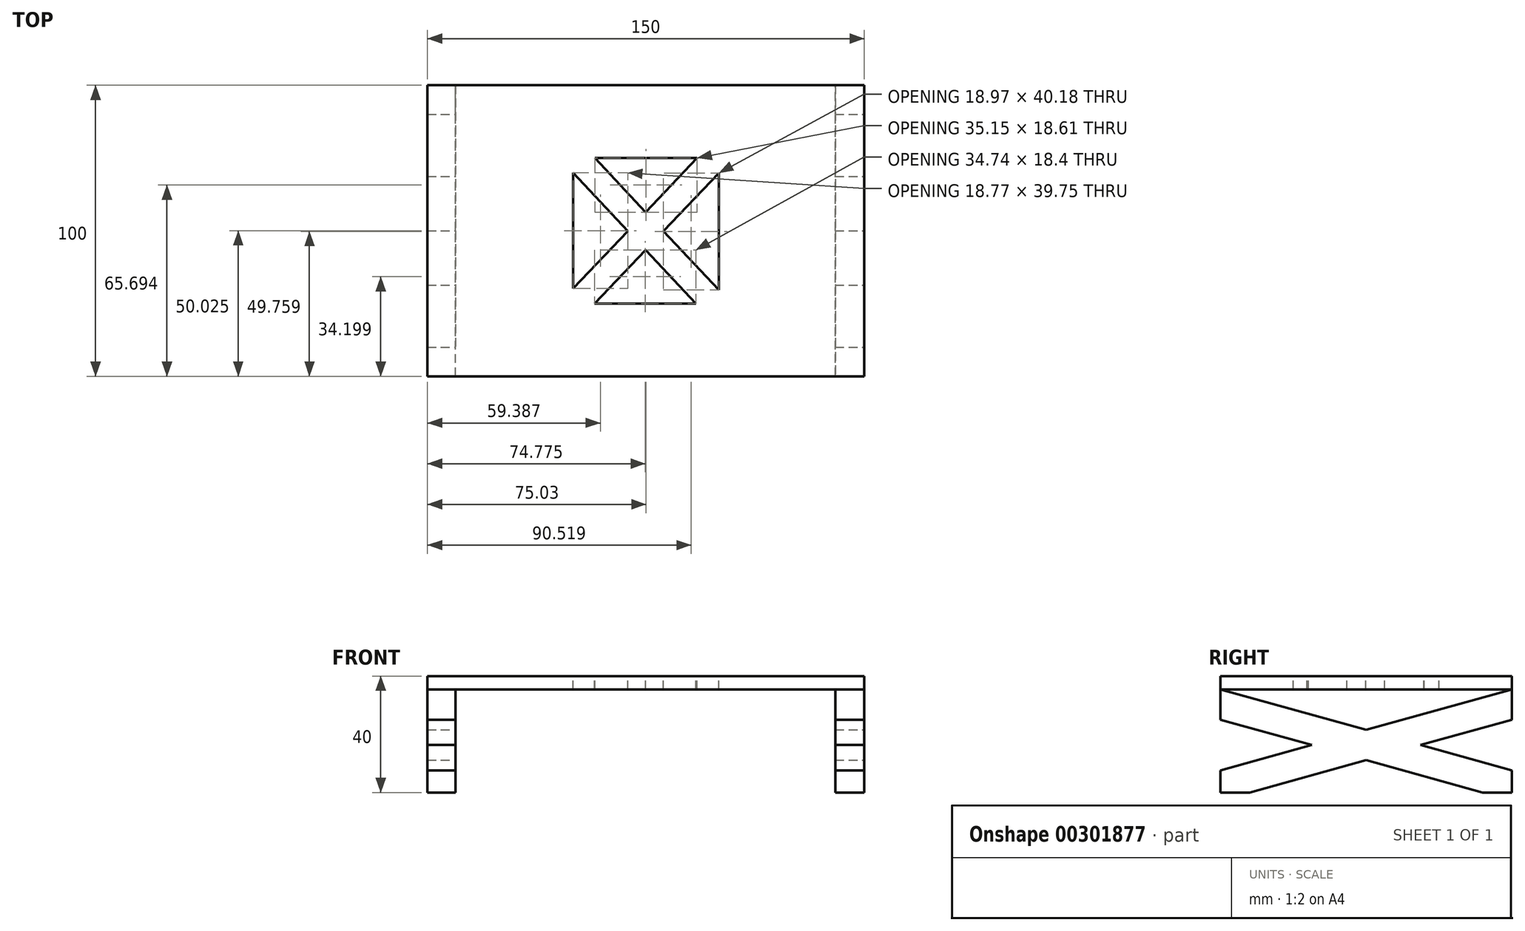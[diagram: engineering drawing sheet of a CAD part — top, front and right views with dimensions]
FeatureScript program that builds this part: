
annotation { "Feature Type Name" : "Feature", "Feature Type Description" : "" }
export const myFeature = defineFeature(function(context is Context, id is Id, definition is map)
    precondition{}
    {
        {
            var Q0;
            Q0=qCreatedBy(makeId("Front.planeOp"),FACE);
            var sketch = newSketch(context, id + "F0", { "sketchPlane" : qUnion([Q0])});
            skLineSegment(sketch, "E0.bottom", {"start": v(-768.36, 54.12) * mm, "end": v(731.64, 54.12) * mm});
            skLineSegment(sketch, "E0.top", {"start": v(-768.36, -345.88) * mm, "end": v(731.64, -345.88) * mm});
            skLineSegment(sketch, "E0.left", {"start": v(-768.36, 54.12) * mm, "end": v(-768.36, -345.88) * mm});
            skLineSegment(sketch, "E0.right", {"start": v(731.64, 54.12) * mm, "end": v(731.64, -345.88) * mm});
            skSolve(sketch);
        }
        {
            var Q0;
            Q0=qSketchRegion(id+"F0",true);
            extrude(context, id + "F1", {"entities" : qUnion([Q0]), "depth" : 1000 * mm});
        }
        {
            var Q0;
            Q0=makeQuery(id+"F1.opExtrude","SWEPT_FACE",FACE,{"disambiguationData":[OSD([sQuery(id+"F0.wireOp",EDGE,"E0.right")])]});
            var sketch = newSketch(context, id + "F2", { "sketchPlane" : qUnion([Q0])});
            skLineSegment(sketch, "E1", {"start": v(-900, -345.88) * mm, "end": v(0, -95.88) * mm});
            skLineSegment(sketch, "E2", {"start": v(-1000, -269.87) * mm, "end": v(0, 7.9) * mm});
            skLineSegment(sketch, "E3", {"start": v(-100, -345.88) * mm, "end": v(-1000, -95.88) * mm});
            skLineSegment(sketch, "E4", {"start": v(0, -269.87) * mm, "end": v(-1000, 7.9) * mm});
            skLineSegment(sketch, "E5", {"start": v(-1000, 7.9) * mm, "end": v(0, 7.9) * mm});
            skSolve(sketch);
        }
        {
            var Q0;
            {var subQ0=sQuery(id+"F2.wireOp",EDGE,"E5");Q0=makeQuery(id+"F2.imprint","IMPRINT",FACE,{"disambiguationData":[TD([[makeQuery(id+"F2.imprint","IMPRINT",EDGE,{"derivedFrom":subQ0}),-1.0]])]});}
            var Q1;
            {var subQ0=sQuery(id+"F2.wireOp",EDGE,"E1");var subQ3=sQuery(id+"F2.wireOp",EDGE,"E3");var subQ4=makeQuery(id+"F2.imprint","INTERSECT",VERTEX,{"derivedFrom":[subQ0,subQ3]});Q1=makeQuery(id+"F2.imprint","IMPRINT",FACE,{"disambiguationData":[TD([[makeQuery(id+"F2.imprint","IMPRINT",EDGE,{"disambiguationData":[TD([[subQ4,1.0]])],"derivedFrom":subQ0}),-1.0]])]});}
            var Q2;
            {var subQ0=sQuery(id+"F2.wireOp",EDGE,"E1");var subQ1=makeQuery(id+"F1.opExtrude","CAP_EDGE",EDGE,{"disambiguationData":[OSD([sQuery(id+"F0.wireOp",EDGE,"E0.right")])],"isStart":true});var subQ2=makeQuery(id+"F2.imprint","INTERSECT",VERTEX,{"derivedFrom":[subQ1,subQ0]});Q2=makeQuery(id+"F2.imprint","IMPRINT",FACE,{"disambiguationData":[TD([[makeQuery(id+"F2.imprint","IMPRINT",EDGE,{"disambiguationData":[TD([[subQ2,1.0]])],"derivedFrom":subQ0}),-1.0]])]});}
            var Q3;
            {var subQ0=sQuery(id+"F2.wireOp",EDGE,"E2");var subQ1=makeQuery(id+"F1.opExtrude","CAP_EDGE",EDGE,{"disambiguationData":[OSD([sQuery(id+"F0.wireOp",EDGE,"E0.right")])],"isStart":false});var subQ2=makeQuery(id+"F2.imprint","INTERSECT",VERTEX,{"derivedFrom":[subQ1,subQ0]});Q3=makeQuery(id+"F2.imprint","IMPRINT",FACE,{"disambiguationData":[TD([[makeQuery(id+"F2.imprint","IMPRINT",EDGE,{"disambiguationData":[TD([[subQ2,-1.0]])],"derivedFrom":subQ0}),1.0]])]});}
            extrude(context, id + "F3", {"entities" : qUnion([Q0, Q1, Q2, Q3]), "operationType" : NewBodyOperationType.REMOVE, "endBound" : BoundingType.THROUGH_ALL, "oppositeDirection" : true, "depth" : 150 * mm});
        }
        {
            var Q0;
            Q0=makeQuery(id+"F1.opExtrude","CAP_FACE",FACE,{"disambiguationData":[OSD([sQuery(id+"F0.wireOp",EDGE,"E0.bottom"),sQuery(id+"F0.wireOp",EDGE,"E0.top"),sQuery(id+"F0.wireOp",EDGE,"E0.left"),sQuery(id+"F0.wireOp",EDGE,"E0.right")])],"isStart":false});
            var sketch = newSketch(context, id + "F4", { "sketchPlane" : qUnion([Q0])});
            skLineSegment(sketch, "E6", {"start": v(631.64, -345.88) * mm, "end": v(631.64, 8.12) * mm});
            skLineSegment(sketch, "E7", {"start": v(631.64, 8.12) * mm, "end": v(-668.36, 8.12) * mm});
            skLineSegment(sketch, "E8", {"start": v(-668.36, 8.12) * mm, "end": v(-668.36, -345.88) * mm});
            skSolve(sketch);
        }
        {
            var Q0;
            {var subQ0=sQuery(id+"F0.wireOp",EDGE,"E0.bottom");var subQ1=sQuery(id+"F0.wireOp",EDGE,"E0.right");var subQ2=sQuery(id+"F0.wireOp",EDGE,"E0.left");Q0=makeQuery(id+"F3.boolean.opBoolean","SPLIT",FACE,{"disambiguationData":[TD([makeQuery(id+"F1.opExtrude","SWEPT_FACE",FACE,{"disambiguationData":[OSD([subQ0])]})])],"derivedFrom":makeQuery(id+"F1.opExtrude","CAP_FACE",FACE,{"disambiguationData":[OSD([subQ0,sQuery(id+"F0.wireOp",EDGE,"E0.top"),subQ2,subQ1])],"isStart":true})});}
            var sketch = newSketch(context, id + "F5", { "sketchPlane" : qUnion([Q0])});
            skLineSegment(sketch, "E9.bottom", {"start": v(-631.78, 7.9) * mm, "end": v(672.17, 7.9) * mm});
            skLineSegment(sketch, "E9.top", {"start": v(-631.78, -349.34) * mm, "end": v(672.17, -349.34) * mm});
            skLineSegment(sketch, "E9.left", {"start": v(-631.78, 7.9) * mm, "end": v(-631.78, -349.34) * mm});
            skLineSegment(sketch, "E9.right", {"start": v(672.17, 7.9) * mm, "end": v(672.17, -349.34) * mm});
            skSolve(sketch);
        }
        {
            var Q0;
            Q0=makeQuery(id+"F5.imprint","IMPRINT",FACE,{"disambiguationData":[TD([[makeQuery(id+"F5.imprint","IMPRINT",EDGE,{"derivedFrom":sQuery(id+"F5.wireOp",EDGE,"E9.bottom")}),1.0]])]});
            extrude(context, id + "F6", {"entities" : qUnion([Q0]), "operationType" : NewBodyOperationType.REMOVE, "endBound" : BoundingType.THROUGH_ALL, "oppositeDirection" : true, "depth" : 25 * mm});
        }
        {
            var Q0;
            Q0=makeQuery(id+"F1.opExtrude","SWEPT_FACE",FACE,{"disambiguationData":[OSD([sQuery(id+"F0.wireOp",EDGE,"E0.bottom")])]});
            var sketch = newSketch(context, id + "F7", { "sketchPlane" : qUnion([Q0])});
            skLineSegment(sketch, "E10.bottom", {"start": v(231.64, -250) * mm, "end": v(-268.36, -250) * mm});
            skLineSegment(sketch, "E10.top", {"start": v(231.64, -750) * mm, "end": v(-268.36, -750) * mm});
            skLineSegment(sketch, "E10.left", {"start": v(231.64, -250) * mm, "end": v(231.64, -750) * mm});
            skLineSegment(sketch, "E10.right", {"start": v(-268.36, -250) * mm, "end": v(-268.36, -750) * mm});
            skLineSegment(sketch, "E11", {"start": v(231.64, -301.5) * mm, "end": v(-194.36, -750) * mm});
            skLineSegment(sketch, "E12", {"start": v(157.64, -250) * mm, "end": v(-268.36, -698.5) * mm});
            skLineSegment(sketch, "E13", {"start": v(-193.84, -250) * mm, "end": v(231.64, -703.32) * mm});
            skLineSegment(sketch, "E14", {"start": v(-268.36, -301) * mm, "end": v(153.06, -750) * mm});
            skSolve(sketch);
        }
        {
            var Q0;
            {var subQ0=sQuery(id+"F7.wireOp",EDGE,"E11");var subQ1=sQuery(id+"F7.wireOp",EDGE,"E10.left");var subQ2=makeQuery(id+"F7.imprint","INTERSECT",VERTEX,{"derivedFrom":[subQ1,subQ0]});Q0=makeQuery(id+"F7.imprint","IMPRINT",FACE,{"disambiguationData":[TD([[makeQuery(id+"F7.imprint","IMPRINT",EDGE,{"disambiguationData":[TD([[subQ2,-1.0]])],"derivedFrom":subQ1}),-1.0]])]});}
            var Q1;
            {var subQ0=sQuery(id+"F7.wireOp",EDGE,"E11");var subQ1=sQuery(id+"F7.wireOp",EDGE,"E10.top");var subQ2=makeQuery(id+"F7.imprint","INTERSECT",VERTEX,{"derivedFrom":[subQ1,subQ0]});Q1=makeQuery(id+"F7.imprint","IMPRINT",FACE,{"disambiguationData":[TD([[makeQuery(id+"F7.imprint","IMPRINT",EDGE,{"disambiguationData":[TD([[subQ2,1.0]])],"derivedFrom":subQ1}),-1.0]])]});}
            var Q2;
            {var subQ0=sQuery(id+"F7.wireOp",EDGE,"E12");var subQ1=sQuery(id+"F7.wireOp",EDGE,"E10.right");var subQ2=makeQuery(id+"F7.imprint","INTERSECT",VERTEX,{"derivedFrom":[subQ1,subQ0]});Q2=makeQuery(id+"F7.imprint","IMPRINT",FACE,{"disambiguationData":[TD([[makeQuery(id+"F7.imprint","IMPRINT",EDGE,{"disambiguationData":[TD([[subQ2,1.0]])],"derivedFrom":subQ1}),1.0]])]});}
            var Q3;
            {var subQ0=sQuery(id+"F7.wireOp",EDGE,"E12");var subQ1=sQuery(id+"F7.wireOp",EDGE,"E10.bottom");var subQ2=makeQuery(id+"F7.imprint","INTERSECT",VERTEX,{"derivedFrom":[subQ1,subQ0]});Q3=makeQuery(id+"F7.imprint","IMPRINT",FACE,{"disambiguationData":[TD([[makeQuery(id+"F7.imprint","IMPRINT",EDGE,{"disambiguationData":[TD([[subQ2,-1.0]])],"derivedFrom":subQ1}),1.0]])]});}
            extrude(context, id + "F8", {"entities" : qUnion([Q0, Q1, Q2, Q3]), "operationType" : NewBodyOperationType.REMOVE, "endBound" : BoundingType.THROUGH_ALL, "oppositeDirection" : true, "depth" : 25 * mm});
        }
        {
            var Q0;
            Q0=makeQuery(id+"F6.boolean.opBoolean","SPLIT",BODY,{"disambiguationData":[OD(1.0)],"derivedFrom":makeQuery(id+"F3.boolean.opBoolean","SPLIT",BODY,{"disambiguationData":[OD(1.0)],"derivedFrom":makeQuery(id+"F1.opExtrude","SWEPT_BODY",BODY,{"disambiguationData":[OSD([sQuery(id+"F0.wireOp",EDGE,"E0.bottom"),sQuery(id+"F0.wireOp",EDGE,"E0.top"),sQuery(id+"F0.wireOp",EDGE,"E0.left"),sQuery(id+"F0.wireOp",EDGE,"E0.right")])]})})});
            var Q1;
            Q1=makeQuery(id+"F6.boolean.opBoolean","SPLIT",BODY,{"disambiguationData":[OD(0.0)],"derivedFrom":makeQuery(id+"F3.boolean.opBoolean","SPLIT",BODY,{"disambiguationData":[OD(1.0)],"derivedFrom":makeQuery(id+"F1.opExtrude","SWEPT_BODY",BODY,{"disambiguationData":[OSD([sQuery(id+"F0.wireOp",EDGE,"E0.bottom"),sQuery(id+"F0.wireOp",EDGE,"E0.top"),sQuery(id+"F0.wireOp",EDGE,"E0.left"),sQuery(id+"F0.wireOp",EDGE,"E0.right")])]})})});
            var Q2;
            Q2=makeQuery(id+"F3.boolean.opBoolean","SPLIT",BODY,{"disambiguationData":[OD(0.0)],"derivedFrom":makeQuery(id+"F1.opExtrude","SWEPT_BODY",BODY,{"disambiguationData":[OSD([sQuery(id+"F0.wireOp",EDGE,"E0.bottom"),sQuery(id+"F0.wireOp",EDGE,"E0.top"),sQuery(id+"F0.wireOp",EDGE,"E0.left"),sQuery(id+"F0.wireOp",EDGE,"E0.right")])]})});
            var Q3;
            Q3=qCreatedBy(makeId("Origin.pointOp"),VERTEX);
            transform(context, id + "F9", {"entities" : qUnion([Q0, Q1, Q2]), "transformType" : TransformType.SCALE_UNIFORMLY, "scale" : 0.1, "scalePoint" : qUnion([Q3]), "makeCopy" : false});
        }
    });
